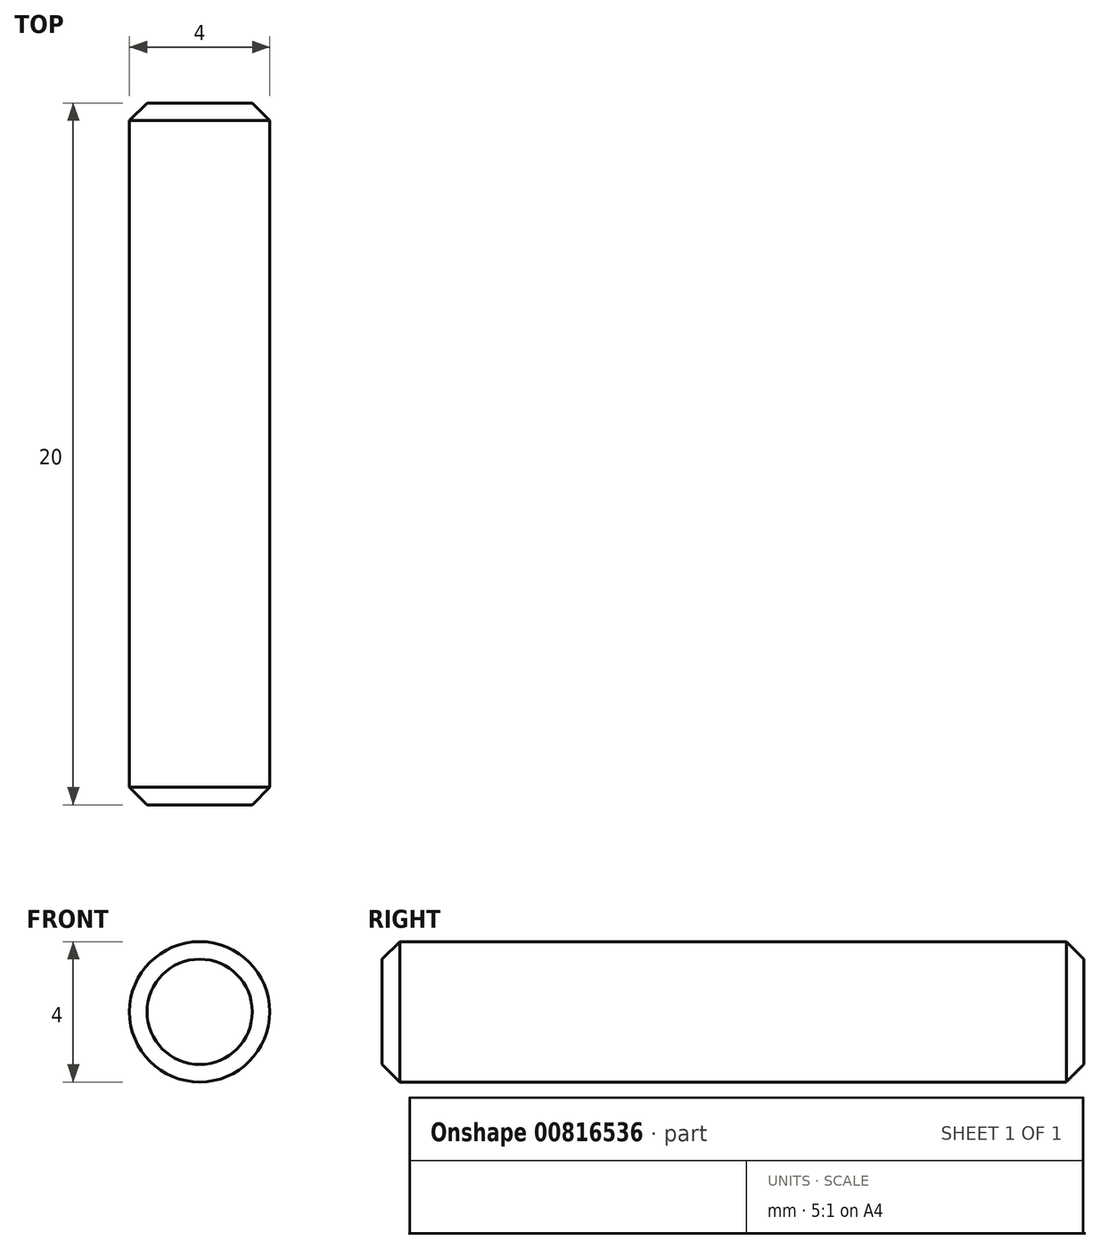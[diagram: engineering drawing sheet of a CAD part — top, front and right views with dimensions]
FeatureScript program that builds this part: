
annotation { "Feature Type Name" : "Feature", "Feature Type Description" : "" }
export const myFeature = defineFeature(function(context is Context, id is Id, definition is map)
    precondition{}
    {
        {
            assignVariable(context, id + "F0", {"name" : "Bolzenlaenge", "anyValue" : 20});
        }
        {
            var Q0;
            Q0=qCreatedBy(makeId("Front.planeOp"),FACE);
            var sketch = newSketch(context, id + "F1", { "sketchPlane" : qUnion([Q0])});
            skCircle(sketch, "E0", {"center": v(0, 0) * mm, "radius": 2 * mm});
            skSolve(sketch);
        }
        {
            var Q0;
            Q0=makeQuery(id+"F1.imprint","IMPRINT",FACE,{"disambiguationData":[TD([[makeQuery(id+"F1.imprint","IMPRINT",EDGE,{"derivedFrom":sQuery(id+"F1.wireOp",EDGE,"E0")}),1.0]])]});
            extrude(context, id + "F2", {"entities" : qUnion([Q0]), "depth" : (getVariable(context, 'Bolzenlaenge')) * mm, "offsetDistance" : 25 * mm});
        }
        {
            var Q0;
            Q0=makeQuery(id+"F2.opExtrude","CAP_EDGE",EDGE,{"disambiguationData":[OSD([sQuery(id+"F1.wireOp",EDGE,"E0")])],"isStart":false});
            var Q1;
            Q1=makeQuery(id+"F2.opExtrude","CAP_FACE",FACE,{"disambiguationData":[OSD([sQuery(id+"F1.wireOp",EDGE,"E0")])],"isStart":true});
            chamfer(context, id + "F3", {"entities" : qUnion([Q0, Q1]), "width" : 0.5 * mm, "tangentPropagation" : true});
        }
    });
